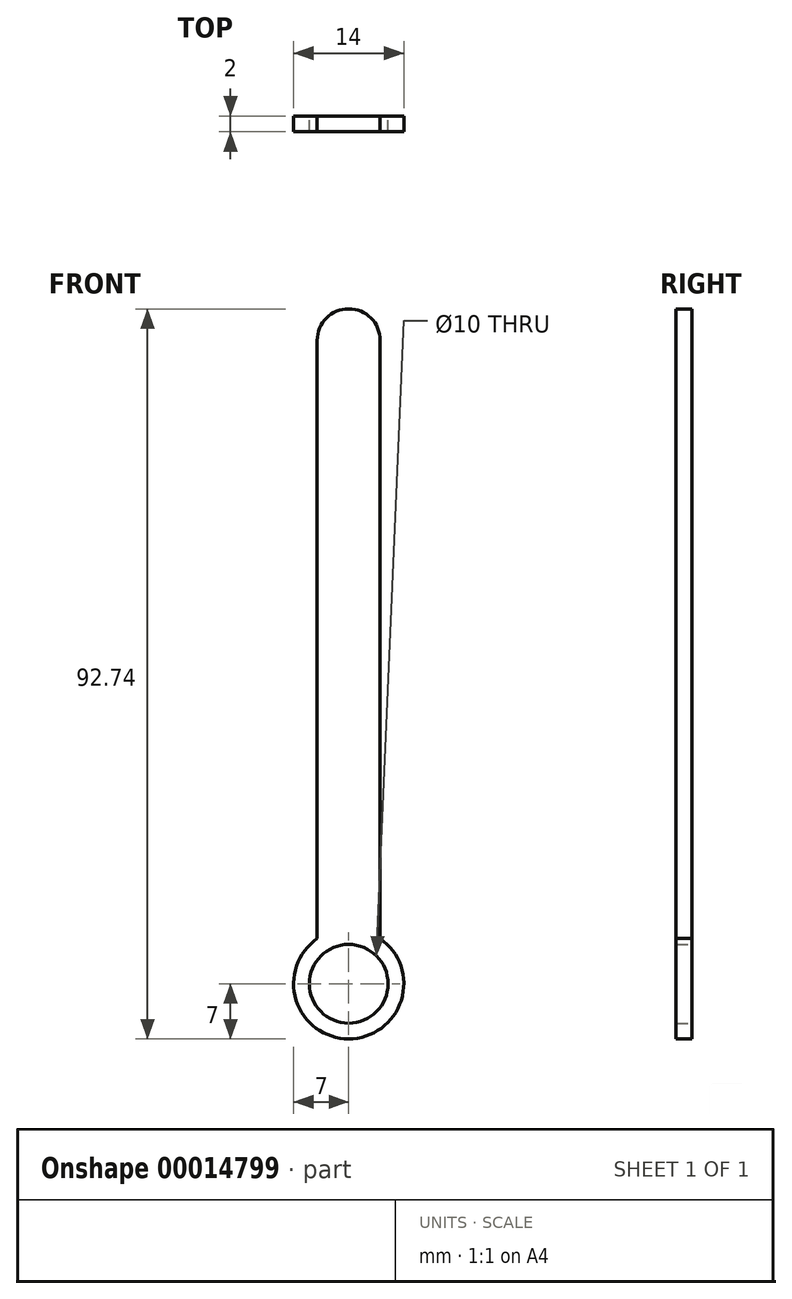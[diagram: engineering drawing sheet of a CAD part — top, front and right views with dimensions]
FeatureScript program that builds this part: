
annotation { "Feature Type Name" : "Feature", "Feature Type Description" : "" }
export const myFeature = defineFeature(function(context is Context, id is Id, definition is map)
    precondition{}
    {
        {
            var Q0;
            Q0=qCreatedBy(makeId("Front.planeOp"),FACE);
            var sketch = newSketch(context, id + "F0", { "sketchPlane" : qUnion([Q0])});
            skCircle(sketch, "E0", {"center": v(0, 0) * mm, "radius": 5 * mm});
            skCircle(sketch, "E1.0", {"center": v(0, 0) * mm, "radius": 7 * mm});
            skLineSegment(sketch, "E2", {"start": v(-4, 5.74) * mm, "end": v(-4, 81.74) * mm});
            skLineSegment(sketch, "E3", {"start": v(-4, 85.74) * mm, "end": v(0, 85.74) * mm, "construction": true});
            skLineSegment(sketch, "E4.0.MirrorCS", {"start": v(4, 5.74) * mm, "end": v(4, 81.74) * mm});
            skLineSegment(sketch, "E5.0.MirrorCS", {"start": v(4, 85.74) * mm, "end": v(0, 85.74) * mm, "construction": true});
            skLineSegment(sketch, "E6", {"start": v(0, 85.74) * mm, "end": v(0, 85.74) * mm});
            skPoint(sketch, "E7.visualSharp", {"position": v(-4, 85.74) * mm});
            skArc(sketch, "E7.filletArc", {"start": v(0, 85.74) * mm, "mid": v(-2.83, 84.57) * mm, "end": v(-4, 81.74) * mm});
            skPoint(sketch, "E8.visualSharp", {"position": v(4, 85.74) * mm});
            skArc(sketch, "E8.filletArc", {"start": v(4, 81.74) * mm, "mid": v(2.83, 84.57) * mm, "end": v(0, 85.74) * mm});
            skSolve(sketch);
        }
        {
            var Q0;
            Q0 = qSketchRegion(id + "F0", true);
            extrude(context, id + "F1", {"entities" : qUnion([Q0]), "depth" : 2 * mm});
        }
    });
